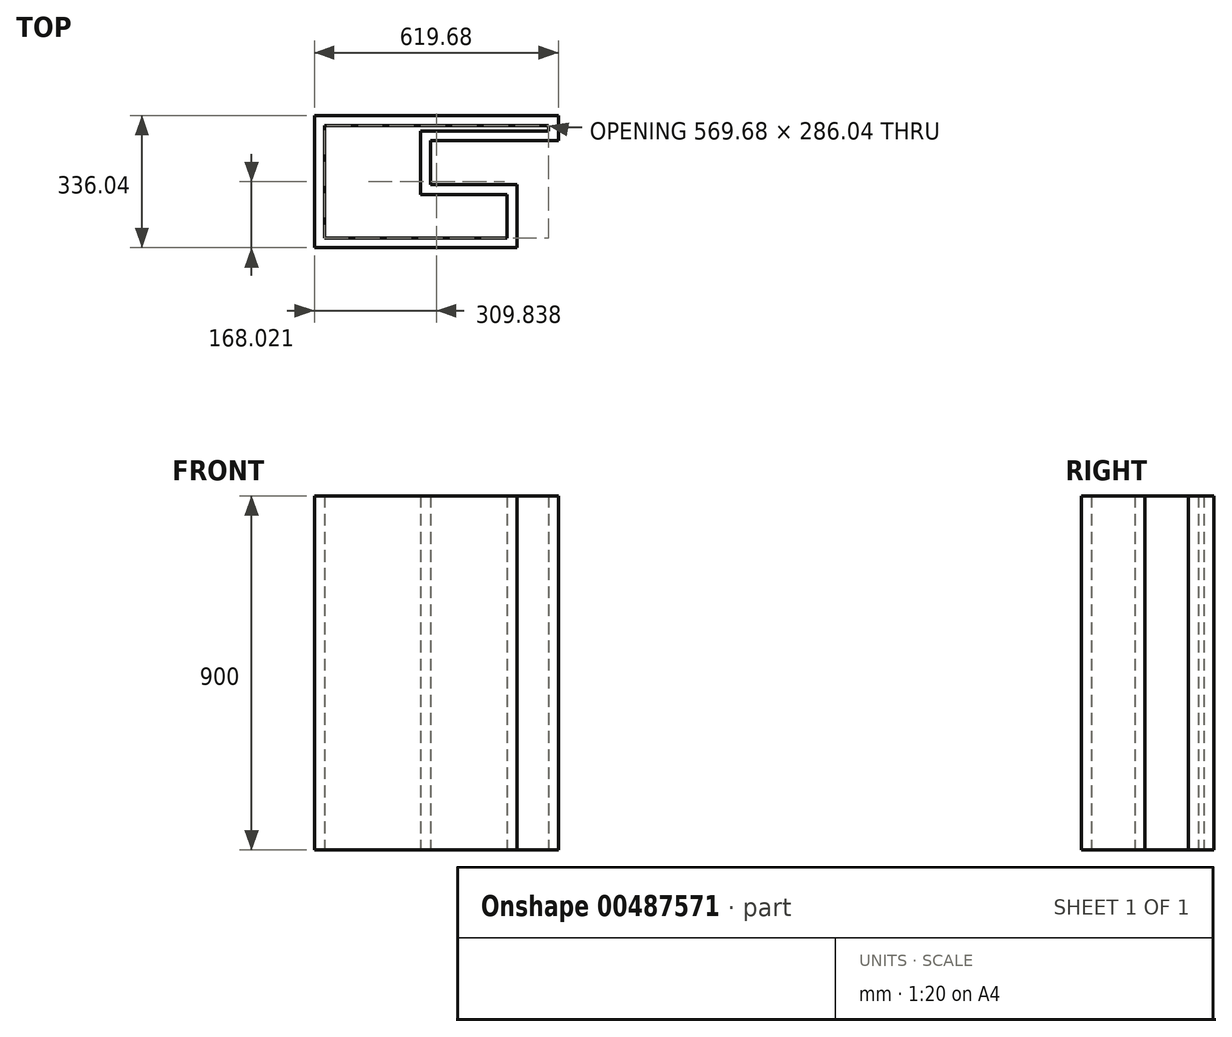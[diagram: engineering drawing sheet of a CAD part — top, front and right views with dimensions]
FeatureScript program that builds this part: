
annotation { "Feature Type Name" : "Feature", "Feature Type Description" : "" }
export const myFeature = defineFeature(function(context is Context, id is Id, definition is map)
    precondition{}
    {
        {
            var Q0;
            Q0=qCreatedBy(makeId("Top.planeOp"),FACE);
            var sketch = newSketch(context, id + "F0", { "sketchPlane" : qUnion([Q0])});
            skLineSegment(sketch, "E0", {"start": v(-40.75, 63.76) * mm, "end": v(209.25, 63.76) * mm});
            skLineSegment(sketch, "E1", {"start": v(9.25, -96.24) * mm, "end": v(9.25, -16.24) * mm});
            skLineSegment(sketch, "E2", {"start": v(-0.75, -16.24) * mm, "end": v(9.25, -16.24) * mm});
            skLineSegment(sketch, "E3", {"start": v(-0.75, -16.24) * mm, "end": v(-0.75, 33.76) * mm});
            skLineSegment(sketch, "E4", {"start": v(-0.75, 33.76) * mm, "end": v(-60.75, 33.76) * mm});
            skLineSegment(sketch, "E5", {"start": v(-60.75, 33.76) * mm, "end": v(-90.75, 33.76) * mm});
            skLineSegment(sketch, "E6", {"start": v(-90.75, 33.76) * mm, "end": v(-90.75, 63.76) * mm});
            skLineSegment(sketch, "E7", {"start": v(-90.75, 63.76) * mm, "end": v(-40.75, 63.76) * mm});
            skLineSegment(sketch, "E8", {"start": v(9.25, -16.24) * mm, "end": v(9.25, -96.24) * mm});
            skLineSegment(sketch, "E9", {"start": v(9.25, -96.24) * mm, "end": v(509.25, -96.24) * mm});
            skLineSegment(sketch, "E10", {"start": v(509.25, -96.24) * mm, "end": v(509.25, 63.76) * mm});
            skLineSegment(sketch, "E11", {"start": v(509.25, 63.76) * mm, "end": v(209.25, 63.76) * mm});
            skLineSegment(sketch, "E12.MirrorCS", {"start": v(509.25, 63.76) * mm, "end": v(809.25, 63.76) * mm});
            skLineSegment(sketch, "E13.MirrorCS", {"start": v(1009.25, -96.24) * mm, "end": v(509.25, -96.24) * mm});
            skLineSegment(sketch, "E14.MirrorCS", {"start": v(1009.25, -16.24) * mm, "end": v(1009.25, -96.24) * mm});
            skLineSegment(sketch, "E15.MirrorCS", {"start": v(1019.25, 33.76) * mm, "end": v(1079.25, 33.76) * mm});
            skLineSegment(sketch, "E16.MirrorCS", {"start": v(1109.25, 33.76) * mm, "end": v(1109.25, 63.76) * mm});
            skLineSegment(sketch, "E17.MirrorCS", {"start": v(1059.25, 63.76) * mm, "end": v(809.25, 63.76) * mm});
            skLineSegment(sketch, "E18.MirrorCS", {"start": v(1109.25, 63.76) * mm, "end": v(1059.25, 63.76) * mm});
            skLineSegment(sketch, "E19.MirrorCS", {"start": v(1079.25, 33.76) * mm, "end": v(1109.25, 33.76) * mm});
            skLineSegment(sketch, "E20.MirrorCS", {"start": v(1019.25, -16.24) * mm, "end": v(1019.25, 33.76) * mm});
            skLineSegment(sketch, "E21.0", {"start": v(532.19, -96.24) * mm, "end": v(532.19, 63.76) * mm});
            skLineSegment(sketch, "E22.0", {"start": v(509.25, 21.1) * mm, "end": v(809.25, 21.1) * mm});
            skLineSegment(sketch, "E23.bottom", {"start": v(53.82, -258.03) * mm, "end": v(475.32, -258.03) * mm});
            skLineSegment(sketch, "E23.top", {"start": v(53.82, -439.22) * mm, "end": v(475.32, -439.22) * mm});
            skLineSegment(sketch, "E23.left", {"start": v(53.82, -258.03) * mm, "end": v(53.82, -439.22) * mm});
            skLineSegment(sketch, "E23.right", {"start": v(475.32, -258.03) * mm, "end": v(475.32, -439.22) * mm});
            skLineSegment(sketch, "E24.0", {"start": v(83.82, -288.03) * mm, "end": v(445.32, -288.03) * mm});
            skLineSegment(sketch, "E24.1", {"start": v(83.82, -288.03) * mm, "end": v(83.82, -409.22) * mm});
            skLineSegment(sketch, "E24.2", {"start": v(83.82, -409.22) * mm, "end": v(445.32, -409.22) * mm});
            skLineSegment(sketch, "E24.3", {"start": v(445.32, -288.03) * mm, "end": v(445.32, -409.22) * mm});
            skLineSegment(sketch, "E25.0", {"start": v(83.82, -414.22) * mm, "end": v(445.32, -414.22) * mm});
            skFitSpline(sketch, "E26", {"points": [v(498.68, 386.66) * mm, v(914.1, 413.31) * mm, v(1136.31, 504.97) * mm, v(1266.42, 254.06) * mm, v(1411.63, 155.77) * mm, v(1142.2, -24.83) * mm, v(1170.1, 149) * mm, v(956.2, 121.86) * mm, v(388.38, 297.9) * mm, v(498.68, 386.66) * mm]});
            skLineSegment(sketch, "E27", {"start": v(703.17, -561.32) * mm, "end": v(191.9, -561.32) * mm});
            skLineSegment(sketch, "E28", {"start": v(191.9, -561.32) * mm, "end": v(191.9, -897.36) * mm});
            skLineSegment(sketch, "E29", {"start": v(191.9, -897.36) * mm, "end": v(706.13, -897.36) * mm});
            skLineSegment(sketch, "E30", {"start": v(706.13, -897.36) * mm, "end": v(706.13, -736.62) * mm});
            skLineSegment(sketch, "E31", {"start": v(706.13, -736.62) * mm, "end": v(486.38, -736.62) * mm});
            skLineSegment(sketch, "E32", {"start": v(486.38, -736.62) * mm, "end": v(486.38, -625.52) * mm});
            skLineSegment(sketch, "E33", {"start": v(486.38, -625.52) * mm, "end": v(811.58, -625.52) * mm});
            skLineSegment(sketch, "E34", {"start": v(811.58, -625.52) * mm, "end": v(811.58, -561.32) * mm});
            skLineSegment(sketch, "E35", {"start": v(703.17, -561.32) * mm, "end": v(811.58, -561.32) * mm});
            skLineSegment(sketch, "E36.0", {"start": v(703.17, -586.32) * mm, "end": v(786.58, -586.32) * mm});
            skLineSegment(sketch, "E36.1", {"start": v(786.58, -600.52) * mm, "end": v(786.58, -586.32) * mm});
            skLineSegment(sketch, "E36.2", {"start": v(703.17, -586.32) * mm, "end": v(216.9, -586.32) * mm});
            skLineSegment(sketch, "E36.3", {"start": v(461.38, -600.52) * mm, "end": v(786.58, -600.52) * mm});
            skLineSegment(sketch, "E36.4", {"start": v(461.38, -761.62) * mm, "end": v(461.38, -600.52) * mm});
            skLineSegment(sketch, "E36.5", {"start": v(216.9, -586.32) * mm, "end": v(216.9, -872.36) * mm});
            skLineSegment(sketch, "E36.6", {"start": v(216.9, -872.36) * mm, "end": v(681.13, -872.36) * mm});
            skLineSegment(sketch, "E36.7", {"start": v(681.13, -872.36) * mm, "end": v(681.13, -761.62) * mm});
            skLineSegment(sketch, "E36.8", {"start": v(681.13, -761.62) * mm, "end": v(461.38, -761.62) * mm});
            skSolve(sketch);
        }
        {
            var Q0;
            Q0=makeQuery(id+"F0.imprint","IMPRINT",FACE,{"disambiguationData":[TD([[makeQuery(id+"F0.imprint","IMPRINT",EDGE,{"derivedFrom":sQuery(id+"F0.wireOp",EDGE,"E27")}),1.0]])]});
            extrude(context, id + "F1", {"entities" : qUnion([Q0]), "depth" : 900 * mm});
        }
    });
